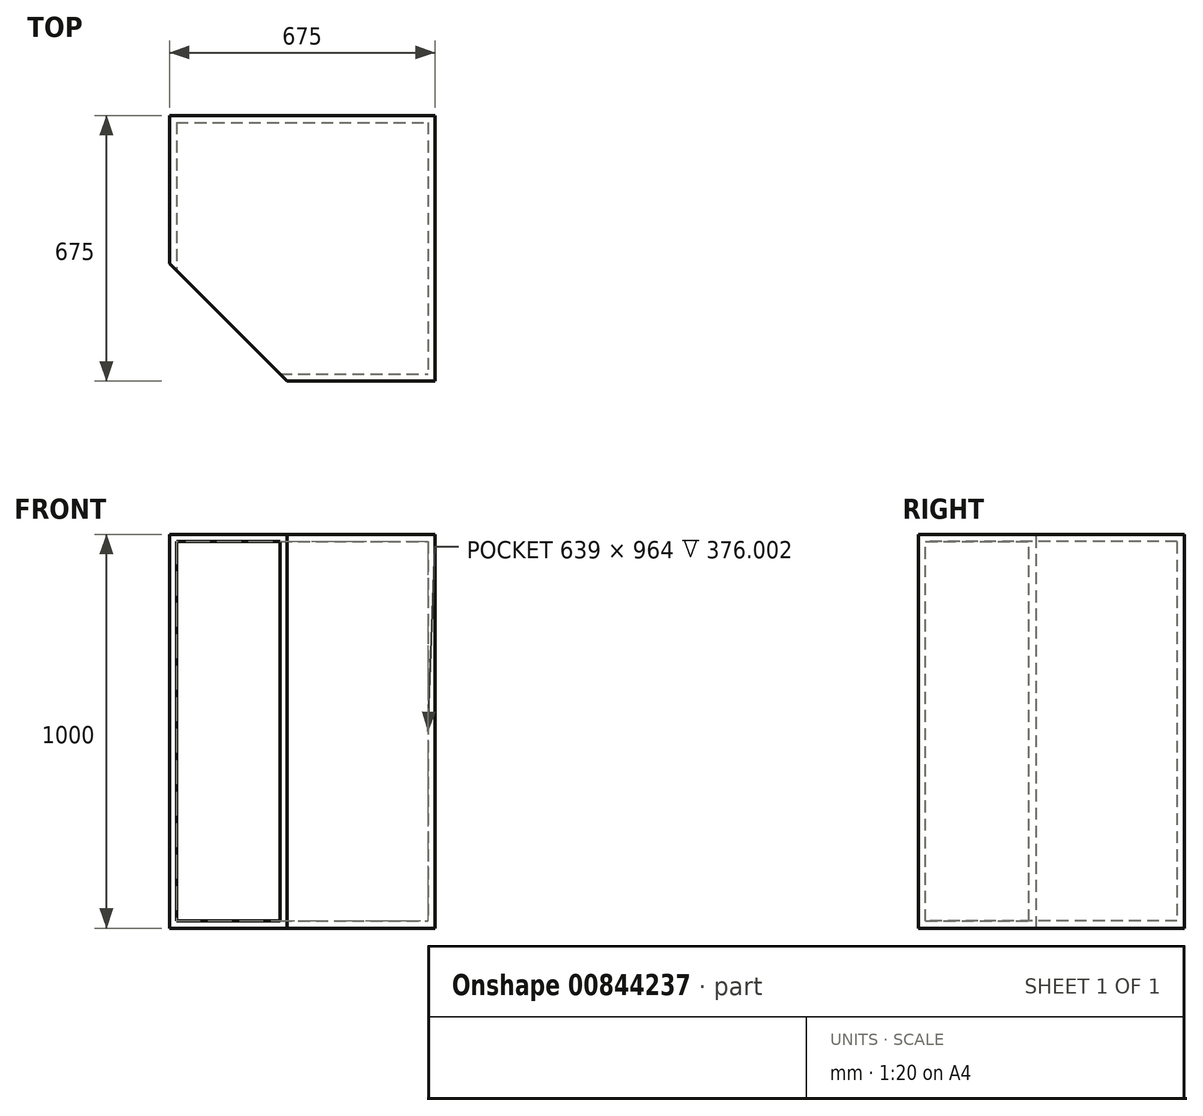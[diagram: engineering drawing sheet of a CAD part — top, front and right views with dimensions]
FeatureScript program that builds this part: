
annotation { "Feature Type Name" : "Feature", "Feature Type Description" : "" }
export const myFeature = defineFeature(function(context is Context, id is Id, definition is map)
    precondition{}
    {
        {
            var Q0;
            Q0=qCreatedBy(makeId("Top.planeOp"),FACE);
            var sketch = newSketch(context, id + "F0", { "sketchPlane" : qUnion([Q0])});
            skLineSegment(sketch, "E0.bottom", {"start": v(0, 0) * mm, "end": v(82.22, 0) * mm});
            skLineSegment(sketch, "E0.top", {"start": v(0, -71.07) * mm, "end": v(82.22, -71.07) * mm});
            skLineSegment(sketch, "E0.left", {"start": v(0, 0) * mm, "end": v(0, -71.07) * mm});
            skLineSegment(sketch, "E0.right", {"start": v(82.22, 0) * mm, "end": v(82.22, -71.07) * mm});
            skSolve(sketch);
        }
        {
            var Q0;
            Q0=makeQuery(id+"F0.imprint","IMPRINT",FACE,{"disambiguationData":[TD([[makeQuery(id+"F0.imprint","IMPRINT",EDGE,{"derivedFrom":sQuery(id+"F0.wireOp",EDGE,"E0.bottom")}),-1.0]])]});
            extrude(context, id + "F1", {"entities" : qUnion([Q0]), "depth" : 1000 * mm, "offsetDistance" : 25 * mm});
        }
        {
            var Q0;
            Q0=makeQuery(id+"F1.opExtrude","SWEPT_FACE",FACE,{"disambiguationData":[OSD([sQuery(id+"F0.wireOp",EDGE,"E0.left")])]});
            extrude(context, id + "F2", {"entities" : qUnion([Q0]), "operationType" : NewBodyOperationType.ADD, "oppositeDirection" : true, "depth" : 675 * mm, "offsetDistance" : 25 * mm});
        }
        {
            var Q0;
            {var subQ0=sQuery(id+"F0.wireOp",EDGE,"E0.bottom");Q0=makeQuery(id+"F2.boolean.opBoolean","MERGE",FACE,{"derivedFrom":[makeQuery(id+"F1.opExtrude","SWEPT_FACE",FACE,{"disambiguationData":[OSD([subQ0])]}),makeQuery(id+"F2.opExtrude","SWEPT_FACE",FACE,{"disambiguationData":[OSD([subQ0,sQuery(id+"F0.wireOp",EDGE,"E0.left")])]})]});}
            extrude(context, id + "F3", {"entities" : qUnion([Q0]), "operationType" : NewBodyOperationType.ADD, "oppositeDirection" : true, "depth" : 675 * mm, "offsetDistance" : 25 * mm});
        }
        {
            var Q0;
            {var subQ0=sQuery(id+"F0.wireOp",EDGE,"E0.left");var subQ1=sQuery(id+"F0.wireOp",EDGE,"E0.bottom");Q0=makeQuery(id+"F3.boolean.opBoolean","MERGE",FACE,{"derivedFrom":[makeQuery(id+"F2.boolean.opBoolean","MERGE",FACE,{"derivedFrom":[makeQuery(id+"F1.opExtrude","CAP_FACE",FACE,{"disambiguationData":[OSD([subQ1,sQuery(id+"F0.wireOp",EDGE,"E0.top"),subQ0,sQuery(id+"F0.wireOp",EDGE,"E0.right")])],"isStart":false}),makeQuery(id+"F2.opExtrude","SWEPT_FACE",FACE,{"disambiguationData":[OSD([subQ0]),TDD([makeQuery(id+"F1.opExtrude","CAP_EDGE",EDGE,{"disambiguationData":[OSD([subQ0])],"isStart":false})])]})]}),makeQuery(id+"F3.opExtrude","SWEPT_FACE",FACE,{"disambiguationData":[OSD([subQ1,subQ0]),TDD([makeQuery(id+"F2.boolean.opBoolean","MERGE",EDGE,{"derivedFrom":[makeQuery(id+"F1.opExtrude","CAP_EDGE",EDGE,{"disambiguationData":[OSD([subQ1])],"isStart":false}),makeQuery(id+"F2.opExtrude","SWEPT_EDGE",EDGE,{"disambiguationData":[OSD([subQ1,subQ0]),TDD([makeQuery(id+"F1.opExtrude","CAP_VERTEX",VERTEX,{"disambiguationData":[OSD([subQ1,subQ0])],"isStart":false})])]})]})])]})]});}
            var sketch = newSketch(context, id + "F4", { "sketchPlane" : qUnion([Q0])});
            skLineSegment(sketch, "E1.bottom", {"start": v(0, -675) * mm, "end": v(383.39, -675) * mm});
            skLineSegment(sketch, "E1.top", {"start": v(0, -326.5) * mm, "end": v(383.39, -326.5) * mm});
            skLineSegment(sketch, "E1.left", {"start": v(0, -675) * mm, "end": v(0, -326.5) * mm});
            skLineSegment(sketch, "E1.right", {"start": v(383.39, -675) * mm, "end": v(383.39, -326.5) * mm});
            skSolve(sketch);
        }
        {
            var Q0;
            Q0=makeQuery(id+"F4.imprint","IMPRINT",FACE,{"disambiguationData":[TD([[makeQuery(id+"F4.imprint","IMPRINT",EDGE,{"derivedFrom":sQuery(id+"F4.wireOp",EDGE,"E1.bottom")}),1.0]])]});
            extrude(context, id + "F5", {"entities" : qUnion([Q0]), "operationType" : NewBodyOperationType.REMOVE, "oppositeDirection" : true, "depth" : 25 * mm, "offsetDistance" : 25 * mm});
        }
        {
            var Q0;
            Q0=makeQuery(id+"F5.boolean.opBoolean","COPY",FACE,{"derivedFrom":makeQuery(id+"F5.opExtrude","SWEPT_FACE",FACE,{"disambiguationData":[OSD([sQuery(id+"F4.wireOp",EDGE,"E1.right")])]})});
            extrude(context, id + "F6", {"entities" : qUnion([Q0]), "operationType" : NewBodyOperationType.ADD, "depth" : 84.39 * mm, "offsetDistance" : 25 * mm});
        }
        {
            var Q0;
            Q0=makeQuery(id+"F5.boolean.opBoolean","COPY",FACE,{"derivedFrom":makeQuery(id+"F5.opExtrude","SWEPT_FACE",FACE,{"disambiguationData":[OSD([sQuery(id+"F4.wireOp",EDGE,"E1.top")])]})});
            extrude(context, id + "F7", {"entities" : qUnion([Q0]), "operationType" : NewBodyOperationType.ADD, "depth" : 49.5 * mm, "offsetDistance" : 25 * mm});
        }
        {
            var Q0;
            Q0=makeQuery(id+"F5.boolean.opBoolean","COPY",FACE,{"derivedFrom":makeQuery(id+"F5.opExtrude","CAP_FACE",FACE,{"disambiguationData":[OSD([sQuery(id+"F4.wireOp",EDGE,"E1.bottom"),sQuery(id+"F4.wireOp",EDGE,"E1.top"),sQuery(id+"F4.wireOp",EDGE,"E1.left"),sQuery(id+"F4.wireOp",EDGE,"E1.right")])],"isStart":false})});
            var sketch = newSketch(context, id + "F8", { "sketchPlane" : qUnion([Q0])});
            skLineSegment(sketch, "E2", {"start": v(299, -675) * mm, "end": v(0, -376) * mm});
            skSolve(sketch);
        }
        {
            var Q0;
            Q0=makeQuery(id+"F8.imprint","IMPRINT",FACE,{"disambiguationData":[TD([[makeQuery(id+"F8.imprint","IMPRINT",EDGE,{"derivedFrom":sQuery(id+"F8.wireOp",EDGE,"E2")}),-1.0]])]});
            extrude(context, id + "F9", {"entities" : qUnion([Q0]), "operationType" : NewBodyOperationType.ADD, "depth" : 25 * mm, "offsetDistance" : 25 * mm});
        }
        {
            var Q0;
            Q0=makeQuery(id+"F5.boolean.opBoolean","COPY",FACE,{"derivedFrom":makeQuery(id+"F5.opExtrude","CAP_FACE",FACE,{"disambiguationData":[OSD([sQuery(id+"F4.wireOp",EDGE,"E1.bottom"),sQuery(id+"F4.wireOp",EDGE,"E1.top"),sQuery(id+"F4.wireOp",EDGE,"E1.left"),sQuery(id+"F4.wireOp",EDGE,"E1.right")])],"isStart":false})});
            extrude(context, id + "F10", {"entities" : qUnion([Q0]), "operationType" : NewBodyOperationType.REMOVE, "oppositeDirection" : true, "depth" : 975 * mm, "offsetDistance" : 25 * mm});
        }
        {
            var Q0;
            {var subQ0=sQuery(id+"F8.wireOp",EDGE,"E2");Q0=makeQuery(id+"F10.boolean.opBoolean","MERGE",FACE,{"derivedFrom":[makeQuery(id+"F9.opExtrude","SWEPT_FACE",FACE,{"disambiguationData":[OSD([subQ0])]}),makeQuery(id+"F10.opExtrude","SWEPT_FACE",FACE,{"disambiguationData":[OSD([subQ0])]})]});}
            shell(context, id + "F11", {"entities" : qUnion([Q0]), "thickness" : 18 * mm});
        }
    });
